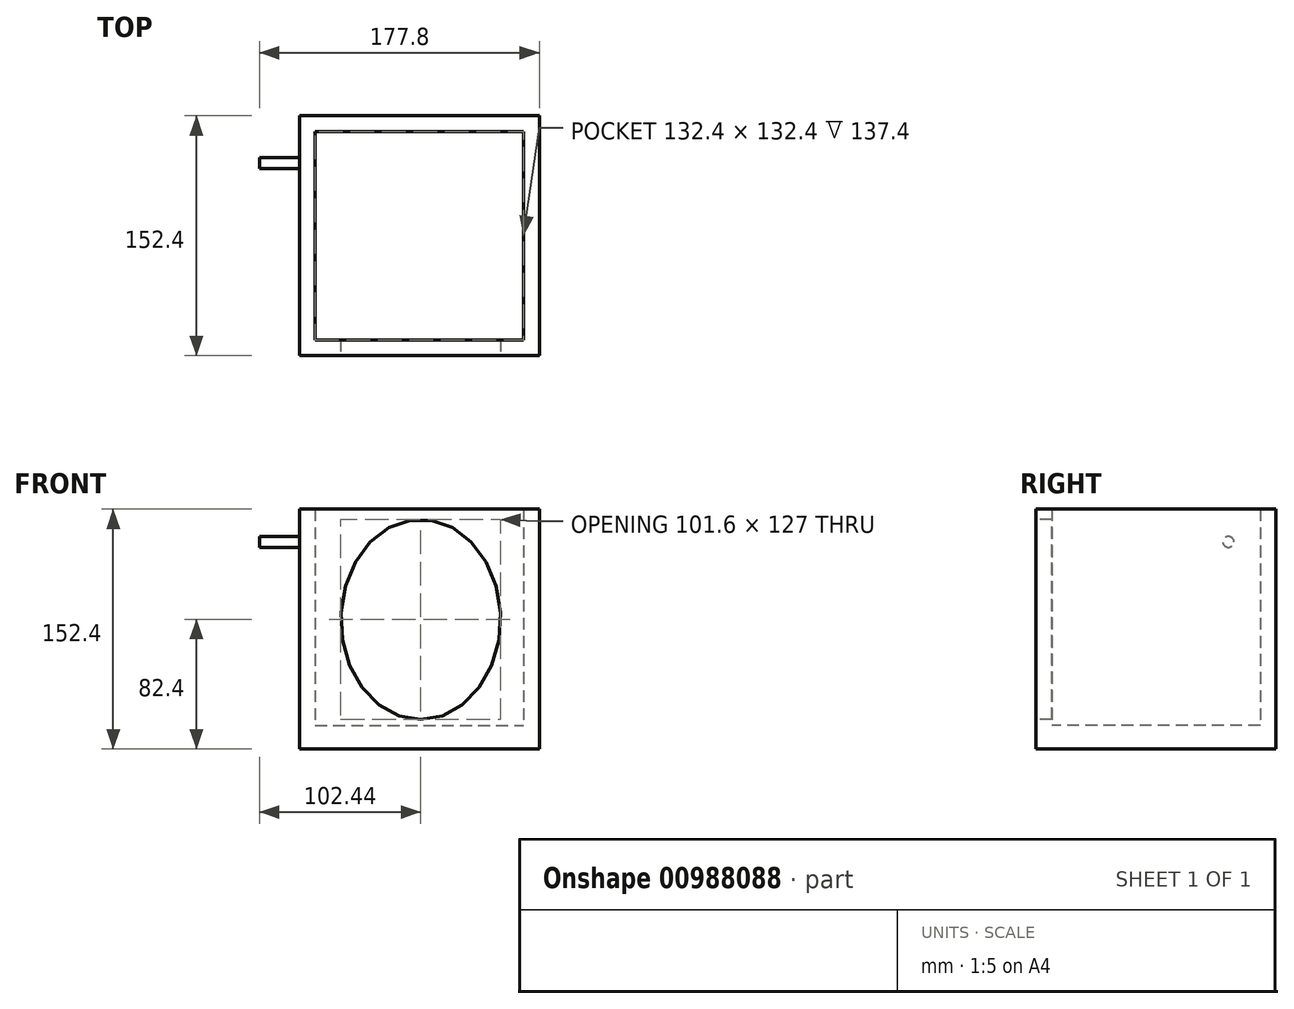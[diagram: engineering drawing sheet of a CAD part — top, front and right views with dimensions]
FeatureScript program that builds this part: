
annotation { "Feature Type Name" : "Feature", "Feature Type Description" : "" }
export const myFeature = defineFeature(function(context is Context, id is Id, definition is map)
    precondition{}
    {
        {
            var Q0;
            Q0=qCreatedBy(makeId("Top.planeOp"),FACE);
            var sketch = newSketch(context, id + "F0", { "sketchPlane" : qUnion([Q0])});
            skLineSegment(sketch, "E0.bottom", {"start": v(-77.04, 108.85) * mm, "end": v(75.36, 108.85) * mm});
            skLineSegment(sketch, "E0.top", {"start": v(-77.04, -43.55) * mm, "end": v(75.36, -43.55) * mm});
            skLineSegment(sketch, "E0.left", {"start": v(-77.04, 108.85) * mm, "end": v(-77.04, -43.55) * mm});
            skLineSegment(sketch, "E0.right", {"start": v(75.36, 108.85) * mm, "end": v(75.36, -43.55) * mm});
            skLineSegment(sketch, "E1.0", {"start": v(-67.04, 98.85) * mm, "end": v(65.36, 98.85) * mm});
            skLineSegment(sketch, "E1.1", {"start": v(-67.04, 98.85) * mm, "end": v(-67.04, -33.55) * mm});
            skLineSegment(sketch, "E1.2", {"start": v(-67.04, -33.55) * mm, "end": v(65.36, -33.55) * mm});
            skLineSegment(sketch, "E1.3", {"start": v(65.36, 98.85) * mm, "end": v(65.36, -33.55) * mm});
            skSolve(sketch);
        }
        {
            var Q0;
            Q0=makeQuery(id+"F0.imprint","IMPRINT",FACE,{"disambiguationData":[TD([[makeQuery(id+"F0.imprint","IMPRINT",EDGE,{"derivedFrom":sQuery(id+"F0.wireOp",EDGE,"E0.bottom")}),-1.0]])]});
            extrude(context, id + "F1", {"entities" : qUnion([Q0]), "depth" : 152.4 * mm, "offsetDistance" : 25 * mm});
        }
        {
            var Q0;
            Q0=makeQuery(id+"F0.imprint","IMPRINT",FACE,{"disambiguationData":[TD([[makeQuery(id+"F0.imprint","IMPRINT",EDGE,{"derivedFrom":sQuery(id+"F0.wireOp",EDGE,"E1.0")}),-1.0]])]});
            extrude(context, id + "F2", {"entities" : qUnion([Q0]), "operationType" : NewBodyOperationType.ADD, "depth" : 15 * mm, "offsetDistance" : 25 * mm});
        }
        {
            var Q0;
            Q0=makeQuery(id+"F1.opExtrude","SWEPT_FACE",FACE,{"disambiguationData":[OSD([sQuery(id+"F0.wireOp",EDGE,"E0.top")])]});
            var sketch = newSketch(context, id + "F3", { "sketchPlane" : qUnion([Q0])});
            skEllipse(sketch, "E2", {"center": v(0, 82.4) * mm, "majorRadius": 63.5 * mm, "minorRadius": 50.8 * mm, "majorAxis": v(0, -1)});
            skLineSegment(sketch, "E3", {"start": v(-52.3, 152.4) * mm, "end": v(60.99, 152.4) * mm});
            skSolve(sketch);
        }
        {
            var Q0;
            Q0=makeQuery(id+"F3.imprint","IMPRINT",FACE,{"disambiguationData":[TD([[makeQuery(id+"F3.imprint","IMPRINT",EDGE,{"derivedFrom":sQuery(id+"F3.wireOp",EDGE,"E2")}),1.0]])]});
            extrude(context, id + "F4", {"entities" : qUnion([Q0]), "operationType" : NewBodyOperationType.REMOVE, "oppositeDirection" : true, "depth" : 25 * mm, "offsetDistance" : 25 * mm});
        }
        {
            var Q0;
            Q0=makeQuery(id+"F1.opExtrude","SWEPT_FACE",FACE,{"disambiguationData":[OSD([sQuery(id+"F0.wireOp",EDGE,"E0.left")])]});
            var sketch = newSketch(context, id + "F5", { "sketchPlane" : qUnion([Q0])});
            skCircle(sketch, "E4", {"center": v(-78.67, 131.65) * mm, "radius": 3.5 * mm});
            skLineSegment(sketch, "E5", {"start": v(-73.56, 152.4) * mm, "end": v(-6.36, 152.4) * mm});
            skSolve(sketch);
        }
        {
            var Q0;
            Q0=makeQuery(id+"F5.imprint","IMPRINT",FACE,{"disambiguationData":[TD([[makeQuery(id+"F5.imprint","IMPRINT",EDGE,{"derivedFrom":sQuery(id+"F5.wireOp",EDGE,"E4")}),1.0]])]});
            extrude(context, id + "F6", {"entities" : qUnion([Q0]), "operationType" : NewBodyOperationType.ADD, "depth" : 25.4 * mm, "offsetDistance" : 25 * mm});
        }
    });
